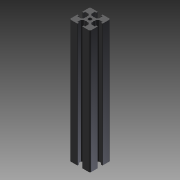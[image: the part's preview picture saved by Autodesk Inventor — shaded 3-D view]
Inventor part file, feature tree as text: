
AUTODESK INVENTOR PART (.ipt)
format: ipt  version: 2011 SP1 (Build 150282100, 282)  size: 144,384 bytes
history: native  units: mm
features: extrude x1, sketch x1
ambient origin geometry x8: Origin, YZ Plane, XZ Plane, XY Plane, X Axis, Y Axis, Z Axis, Center Point
bodies: Solid1 (feature_tree)
feature tree (2):
  extrude  "Extrusion1"  [1 undecoded]
  sketch  "Sketch_1"  dims[d0=90.0mm d1=0.0mm]
note: 1 required parameter value undecoded (feature->parameter linkage not recoverable at this tier; creation-order binding heuristic only, values carry confidence <= 0.55)
